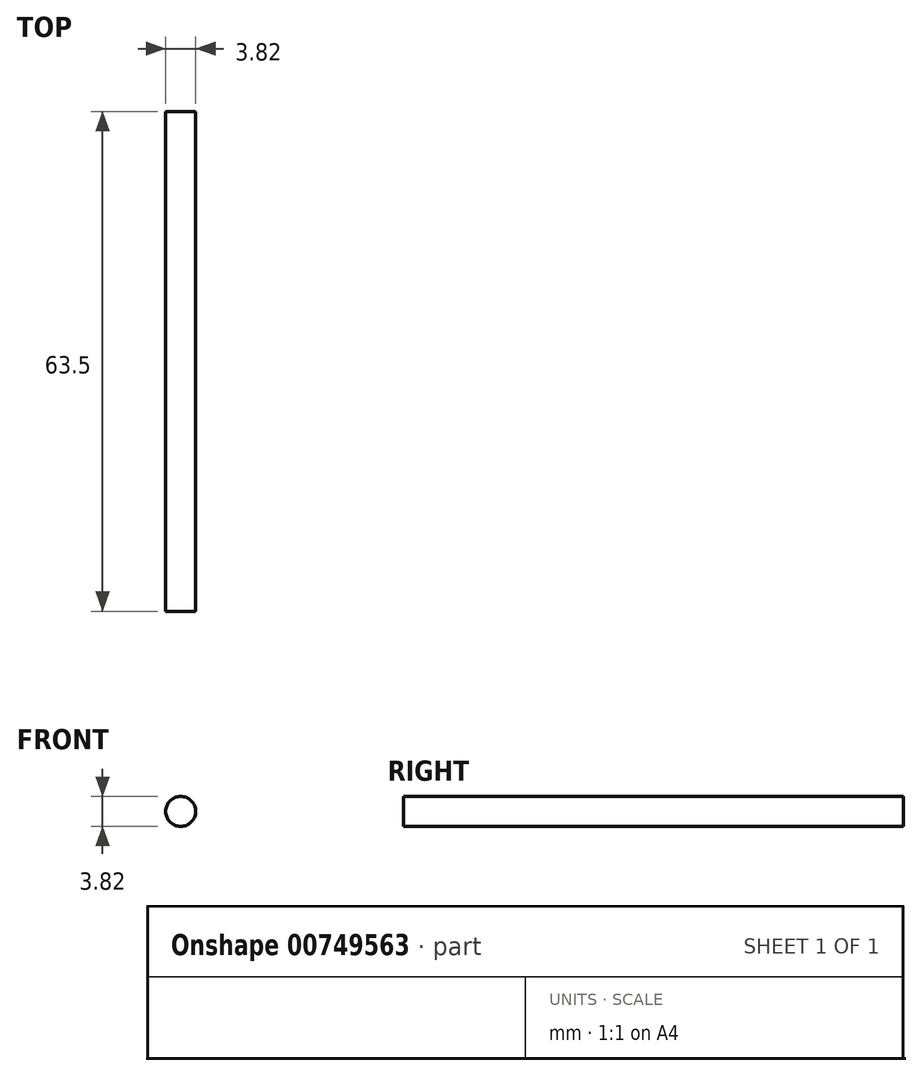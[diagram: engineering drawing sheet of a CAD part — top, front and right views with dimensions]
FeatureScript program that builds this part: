
annotation { "Feature Type Name" : "Feature", "Feature Type Description" : "" }
export const myFeature = defineFeature(function(context is Context, id is Id, definition is map)
    precondition{}
    {
        {
            var Q0;
            Q0=qCreatedBy(makeId("Front.planeOp"),FACE);
            var sketch = newSketch(context, id + "F0", { "sketchPlane" : qUnion([Q0])});
            skCircle(sketch, "E0", {"center": v(0, 0) * mm, "radius": 1.9 * mm});
            skSolve(sketch);
        }
        {
            var Q0;
            Q0=makeQuery(id+"F0.imprint","IMPRINT",FACE,{"disambiguationData":[TD([[makeQuery(id+"F0.imprint","IMPRINT",EDGE,{"derivedFrom":sQuery(id+"F0.wireOp",EDGE,"E0")}),1.0]])]});
            extrude(context, id + "F1", {"entities" : qUnion([Q0]), "depth" : 63.5 * mm, "offsetDistance" : 25.4 * mm});
        }
    });
